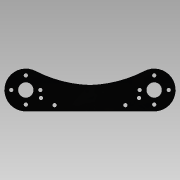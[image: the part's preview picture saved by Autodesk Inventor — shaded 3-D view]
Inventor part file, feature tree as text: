
AUTODESK INVENTOR PART (.ipt)
format: ipt  version: 2015 SP1 (Build 190203100, 203)  size: 115,200 bytes
history: native  units: mm
features: extrude x1, sketch x1
ambient origin geometry x8: Origin, YZ Plane, XZ Plane, XY Plane, X Axis, Y Axis, Z Axis, Center Point
bodies: Body1 (feature_tree)
feature tree (2):
  extrude  "Extrusion3"  Depth=3.5mm
  sketch  "Sketch1"  dims[d47=8.509mm d48=8.509mm d49=8.509mm d50=8.509mm d51=10.0mm d53=9.0mm d56=9.0mm d58=4.19811mm d61=75.0mm d62=3.5mm d63=0.0mm]
